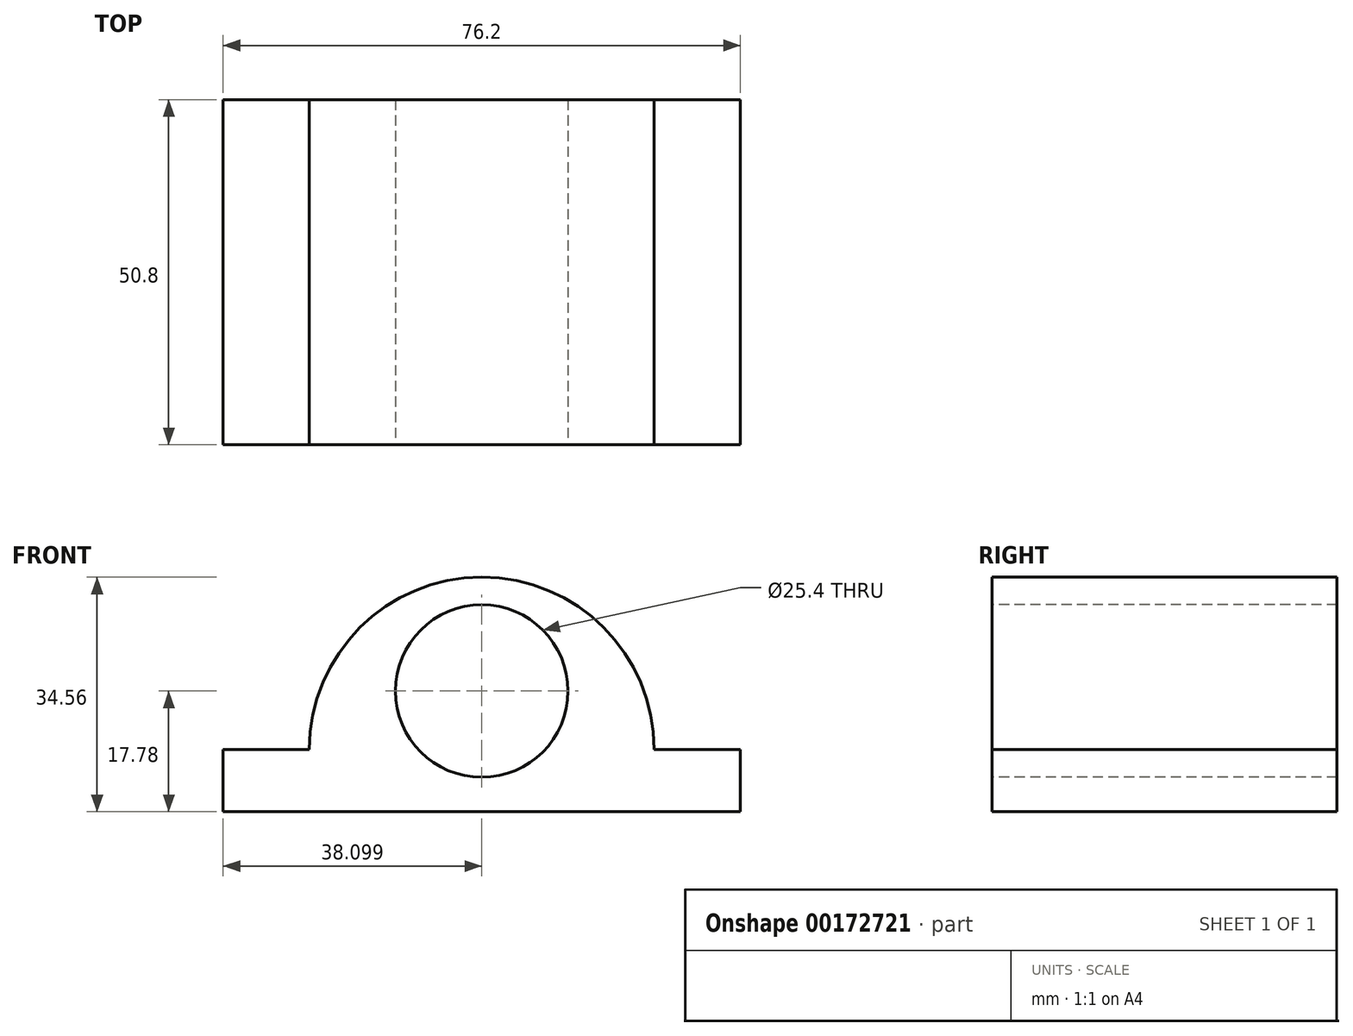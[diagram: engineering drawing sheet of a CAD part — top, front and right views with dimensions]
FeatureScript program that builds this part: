
annotation { "Feature Type Name" : "Feature", "Feature Type Description" : "" }
export const myFeature = defineFeature(function(context is Context, id is Id, definition is map)
    precondition{}
    {
        {
            var Q0;
            Q0=qCreatedBy(makeId("Front.planeOp"),FACE);
            var sketch = newSketch(context, id + "F0", { "sketchPlane" : qUnion([Q0])});
            skLineSegment(sketch, "E0.bottom", {"start": v(-30.25, 9.16) * mm, "end": v(45.95, 9.16) * mm});
            skLineSegment(sketch, "E0.top", {"start": v(-30.25, 0) * mm, "end": v(45.95, 0) * mm});
            skLineSegment(sketch, "E0.left", {"start": v(-30.25, 9.16) * mm, "end": v(-30.25, 0) * mm});
            skLineSegment(sketch, "E0.right", {"start": v(45.95, 9.16) * mm, "end": v(45.95, 0) * mm});
            skSolve(sketch);
        }
        {
            var Q0;
            Q0 = qSketchRegion(id + "F0", true);
            extrude(context, id + "F1", {"entities" : qUnion([Q0]), "depth" : 50.8 * mm});
        }
        {
            var Q0;
            Q0=makeQuery(id+"F1.opExtrude","CAP_FACE",FACE,{"disambiguationData":[OSD([sQuery(id+"F0.wireOp",EDGE,"E0.bottom"),sQuery(id+"F0.wireOp",EDGE,"E0.top"),sQuery(id+"F0.wireOp",EDGE,"E0.left"),sQuery(id+"F0.wireOp",EDGE,"E0.right")])],"isStart":false});
            var sketch = newSketch(context, id + "F2", { "sketchPlane" : qUnion([Q0])});
            skArc(sketch, "E1", {"start": v(33.25, 9.16) * mm, "mid": v(7.85, 34.56) * mm, "end": v(-17.55, 9.16) * mm});
            skSolve(sketch);
        }
        {
            var Q0;
            {var subQ0=sQuery(id+"F2.wireOp",EDGE,"E1");Q0=makeQuery(id+"F2.imprint","IMPRINT",FACE,{"disambiguationData":[TD([[makeQuery(id+"F2.imprint","IMPRINT",EDGE,{"derivedFrom":subQ0}),1.0]])]});}
            extrude(context, id + "F3", {"entities" : qUnion([Q0]), "operationType" : NewBodyOperationType.ADD, "oppositeDirection" : true, "depth" : 50.8 * mm});
        }
        {
            var Q0;
            {var subQ0=sQuery(id+"F0.wireOp",EDGE,"E0.bottom");Q0=makeQuery(id+"F3.boolean.opBoolean","MERGE",FACE,{"derivedFrom":[makeQuery(id+"F1.opExtrude","CAP_FACE",FACE,{"disambiguationData":[OSD([subQ0,sQuery(id+"F0.wireOp",EDGE,"E0.top"),sQuery(id+"F0.wireOp",EDGE,"E0.left"),sQuery(id+"F0.wireOp",EDGE,"E0.right")])],"isStart":false}),makeQuery(id+"F3.opExtrude","CAP_FACE",FACE,{"disambiguationData":[OSD([subQ0,sQuery(id+"F2.wireOp",EDGE,"E1")])],"isStart":true})]});}
            var sketch = newSketch(context, id + "F4", { "sketchPlane" : qUnion([Q0])});
            skCircle(sketch, "E2", {"center": v(7.85, 17.78) * mm, "radius": 12.7 * mm});
            skPoint(sketch, "E2.centerSnap0", {"position": v(7.85, 0) * mm});
            skSolve(sketch);
        }
        {
            var Q0;
            Q0=sQuery(id+"F4.wireOp",VERTEX,"E2.center");
            var Q1;
            Q1=makeQuery(id+"F1.opExtrude","SWEPT_BODY",BODY,{"disambiguationData":[OSD([sQuery(id+"F0.wireOp",EDGE,"E0.bottom"),sQuery(id+"F0.wireOp",EDGE,"E0.top"),sQuery(id+"F0.wireOp",EDGE,"E0.left"),sQuery(id+"F0.wireOp",EDGE,"E0.right")])]});
            hole(context, id + "F5", {"style" : HoleStyle.SIMPLE, "endStyle" : HoleEndStyle.THROUGH, "holeDiameter" : 25.4 * mm, "locations" : qUnion([Q0]), "scope" : qUnion([Q1]), "isTappedThrough" : true});
        }
    });
